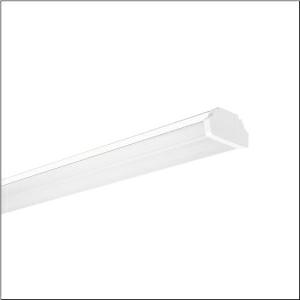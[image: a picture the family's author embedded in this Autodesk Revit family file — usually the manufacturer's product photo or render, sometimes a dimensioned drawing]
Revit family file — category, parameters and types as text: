
# Revit family: dus_31_gen_2_53bd813dv4a5c2_132e
name_source: partatom
category: Lighting Fixtures
units: mm (PartAtom-declared; Revit-internal decimal feet)

## family parameters
Cut with Voids When Loaded = No
Host = Face
Light Source = No
Part Type = Normal
Room Calculation Point = No
Round Connector Dimension = Use Diameter
Shared = No

## types (1)
- --- (1 x LED, 10610 lm, 61.4 W, 4000K)
    Apparent Load = 61 VA
    CIE Flux Codes = 62 83 95 93 100
    Color Rendering = 80
    Color Temperature = 4000K
    Default Elevation = 1800 mm
    Description = DUS 31 Gen.2, luminaire insert, of sheet steel, coil coated, white, length: 1.535mm, width: 81mm, height: 90mm, 5x system unit, system units: 307mm, LED rated luminous flux: 10.610lm, light colour: 840, SDCM (Standard Deviation of Colour Matching)MacAdam ≤ 3 SDCM (initial), control gear: DALI 2, control gear: ECG DALI, with plug, 5-pole, with phase selection, mains connection: 220..240V, AC, 50/60Hz, rated input power: 61W, through-wiring accessed according to module size, primary optical cover: cover, of PMMA, light emission: direct distribution, primary light characteristic: symmetric, protection rating (complete): IP20, protection rating (LED compartment): IP50, insulation class (complete): insulation class I (protective earthing), certification: CE, ENEC, VDE, UKCA, impact resistance: IK03, permissible ambient temperature for indoor applications: -25..+35°C, corresponds to IFS (International Featured Standards) requirements for safety and quality in the food industry, reducing of maximum allowable ambient temperature of 5°C with ceiling mounting, packaging unit: 1 piece
    Height = 95 mm
    Lamp = 1 x LED
    Lamp Light Flux = 10610 lm
    Lamp Power = 61.4 W
    Lamp count = 1
    Length = 1535 mm
    Luminous efficacy = 173 lm/W
    Manufacturer = Siteco
    ModVariant = No
    Model = 53BD813DV4A5C2
    Mounting Place = Ceiling
    Mounting Type = Pendant
    Number of Poles = 1
    OnlyDefault = Yes
    Power Factor = 1
    Product Name = DUS 31 Gen.2
    Product group = luminaire insert | ceiling pendant
    ProductGroupID = 901
    Protection Class = Protection class I
    Protection Degree = IP 20
    RLX_Detail_Level = 1
    RLX_Emergency_Light_Flux = 0 lm
    RLX_Emergency_Type = 0
    RLX_Emergency_Type_DB = No
    RlxData = <blob elided: 32417 chars, md5=937a21db>
    Socket = socket
    Standby Power = 0 W
    System Light Flux = 10610 lm
    System Power = 61 W
    Type Comments = factory setting: luminous flux: 100 % | dim-lin: 254 | 418 mA
    Type Image = l_1319596.jpg
    URL = http://relux.com
    VarID = @adj_051867
    Voltage = 0 V
    Weight = 0.00 kg
    Width = 81 mm

## geometry (parser evidence)
native form markers: Blend x4, Sweep x13
no freeform markers — native parametric forms only
